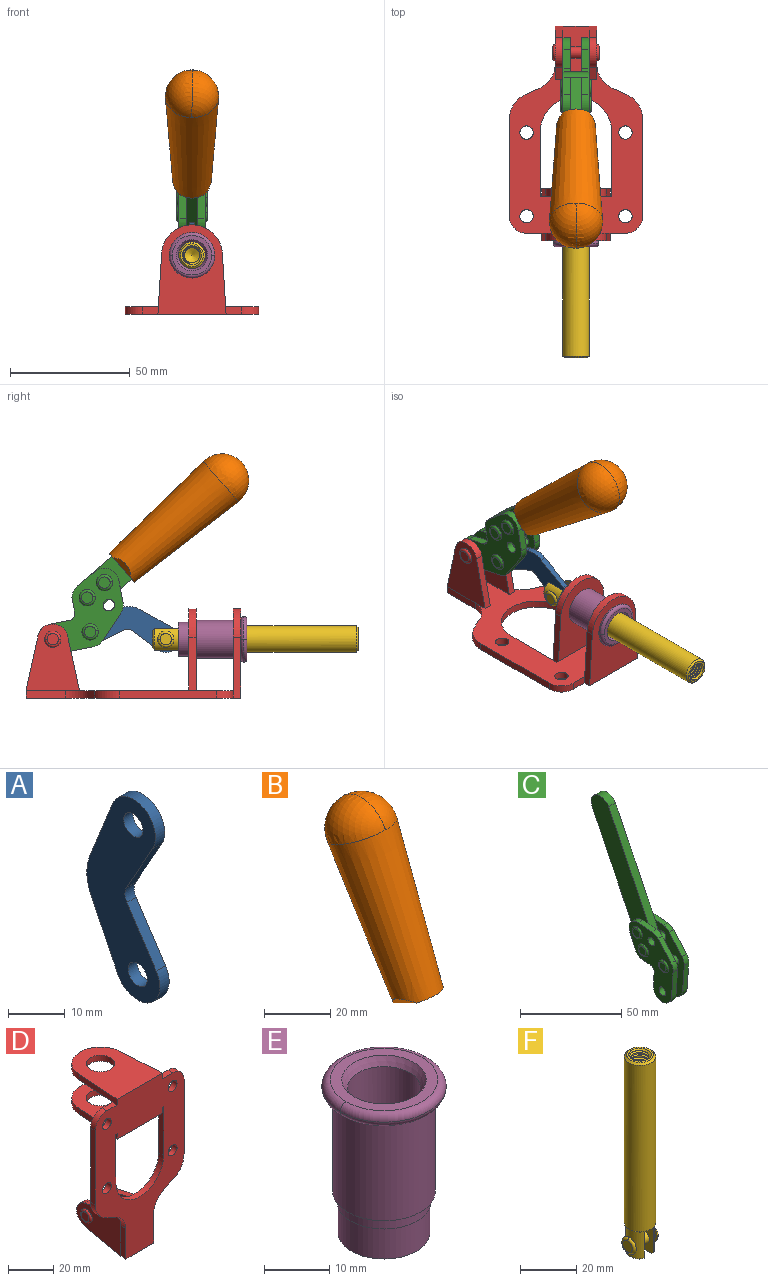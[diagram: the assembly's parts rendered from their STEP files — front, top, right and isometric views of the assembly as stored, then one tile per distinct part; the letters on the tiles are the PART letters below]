
ASSEMBLY  parts=6 mates=6
PART A: 12 faces, bbox 2.3x18.2x42.8 mm
  f0: cylinder r=2.4mm len=4.8mm, axis (1,0,0), area 34.9mm2, adj f4,f11
  f1: cylinder r=10.41mm len=8.47mm, axis (1,0,0), area 20.2mm2, adj f4,f9,f10,f11
  f2: cylinder r=3.05mm len=3.16mm, axis (1,0,0), area 7.7mm2, adj f4,f6,f7,f11
  f3: cylinder r=2.4mm len=4.8mm, axis (1,0,0), area 34.9mm2, adj f4,f11
  f4: plane 42.81x18.23mm, normal (-1,0,0), area 414.1mm2, adj f0,f1,f2,f3,f5,f6,f7,f8
  f5: cylinder r=5.54mm len=10.67mm, axis (1,0,0), area 41.8mm2, adj f4,f6,f10,f11
  f6: plane 11.66x6.53mm, normal (0,-0.87,-0.49), area 30.9mm2, adj f2,f4,f5,f11
  f7: plane 11.17x7.33mm, normal (0,-0.84,0.55), area 30.9mm2, adj f2,f4,f8,f11
  f8: cylinder r=5.54mm len=10.51mm, axis (1,0,0), area 41.8mm2, adj f4,f7,f9,f11
  f9: plane 13.67x6.67mm, normal (0,0.9,-0.44), area 35.1mm2, adj f1,f4,f8,f11
  f10: plane 14.1x5.7mm, normal (0,0.93,0.37), area 35.1mm2, adj f1,f4,f5,f11
  f11: plane 42.81x18.23mm, normal (1,0,0), area 414.1mm2, adj f0,f1,f2,f3,f5,f6,f7,f8
PART B: 11 faces, bbox 22.3x42.6x64.5 mm
  f0: sphere r=11.13mm, area 411.4mm2, adj f1,f8
  f1: cone r=11.11mm half-angle=3.3deg, axis (0,0.44,0.9), area 3251.8mm2, adj f0,f7,f8,f9,f10
  f2: cylinder r=6.16mm len=11.7mm, axis (1,0,0), area 89.5mm2, adj f3,f4,f5,f6
  f3: plane 60.23x36.75mm, normal (-1,0,0), area 763.6mm2, adj f2,f4,f6,f10
  f4: plane 51.37x25.05mm, normal (0,0.9,-0.44), area 264.2mm2, adj f2,f3,f5,f10
  f5: plane 60.23x36.75mm, normal (1,0,0), area 763.6mm2, adj f2,f4,f6,f10
  f6: plane 51.37x25.05mm, normal (0,-0.9,0.44), area 264.2mm2, adj f2,f3,f5,f10
  f7: plane 9.95x5.95mm, normal (0.71,-0.31,-0.64), area 25.8mm2, adj f1,f10
  f8: sphere r=11.13mm, area 411.4mm2, adj f0,f1
  f9: plane 9.95x5.95mm, normal (-0.71,-0.31,-0.64), area 25.8mm2, adj f1,f10
  f10: plane 14.27x11.38mm, normal (0,-0.44,-0.9), area 106.7mm2, adj f1,f3,f4,f5,f6,f7,f9
PART C: 59 faces, bbox 12.9x60.2x99.6 mm
  f0: torus R=2.39mm, axis (-1,0,0), area 14.9mm2, adj f20,f43,f51
  f1: torus R=2.39mm, axis (-1,0,0), area 14.9mm2, adj f19,f42,f51
  f2: torus R=2.39mm, axis (-1,0,0), area 14.9mm2, adj f18,f35,f51
  f3: torus R=2.39mm, axis (-1,0,0), area 14.9mm2, adj f14,f17,f23
  f4: torus R=2.39mm, axis (-1,0,0), area 14.9mm2, adj f13,f16,f23
  f5: torus R=2.39mm, axis (-1,0,0), area 14.9mm2, adj f12,f15,f23
  f6: cylinder r=2.39mm len=4.78mm, axis (1,0,0), area 46.5mm2, adj f48,f50,f51
  f7: cylinder r=2.39mm len=4.78mm, axis (1,0,0), area 46.5mm2, adj f50,f51
  f8: cylinder r=6.35mm len=12.68mm, axis (1,0,0), area 61.8mm2, adj f38,f39,f50,f51
  f9: cylinder r=2.39mm len=4.78mm, axis (-1,0,0), area 70.5mm2, adj f46,f50
  f10: cylinder r=2.39mm len=4.78mm, axis (-1,0,0), area 46.5mm2, adj f23,f45,f46
  f11: cylinder r=2.39mm len=4.78mm, axis (-1,0,0), area 46.5mm2, adj f23,f46
  f12: plane 4.78x4.78mm, normal (1,0,0), area 17.9mm2, adj f5,f15
  f13: plane 4.78x4.78mm, normal (1,0,0), area 17.9mm2, adj f4,f16
  f14: plane 4.78x4.78mm, normal (1,0,0), area 17.9mm2, adj f3,f17
  f15: torus R=2.39mm, axis (-1,0,0), area 14.9mm2, adj f5,f12,f23
  f16: torus R=2.39mm, axis (-1,0,0), area 14.9mm2, adj f4,f13,f23
  f17: torus R=2.39mm, axis (-1,0,0), area 14.9mm2, adj f3,f14,f23
  f18: plane 4.78x4.78mm, normal (-1,0,0), area 17.9mm2, adj f2,f35
  f19: plane 4.78x4.78mm, normal (-1,0,0), area 17.9mm2, adj f1,f42
  f20: plane 4.78x4.78mm, normal (-1,0,0), area 17.9mm2, adj f0,f43
  f21: plane 2.26x0.2mm, normal (1,0,0), area 0.2mm2, adj f31,f44
  f22: plane 2.26x0.2mm, normal (-1,0,0), area 0.2mm2, adj f41,f44
  f23: plane 39.37x30.77mm, normal (1,0,0), area 565.5mm2, adj f3,f4,f5,f10,f11,f15,f16,f17
  f24: cylinder r=6.1mm len=4.15mm, axis (-1,0,0), area 14.7mm2, adj f23,f25,f32,f46
  f25: plane 10.25x9.01mm, normal (0,-0.75,0.66), area 42.3mm2, adj f23,f24,f26,f46
  f26: cylinder r=6.35mm len=4.64mm, axis (-1,0,0), area 15.6mm2, adj f23,f25,f27,f46
  f27: plane 15.84x3.1mm, normal (0,-1,-0.07), area 49.2mm2, adj f23,f26,f28,f46
  f28: cylinder r=6.35mm len=12.68mm, axis (-1,0,0), area 61.8mm2, adj f23,f27,f29,f46
  f29: plane 8.11x3.1mm, normal (0,1,0.07), area 25.2mm2, adj f23,f28,f30,f46
  f30: cylinder r=3.05mm len=3.25mm, axis (-1,0,0), area 14.8mm2, adj f23,f29,f31,f46
  f31: plane 5.99x3.1mm, normal (0,0.07,-1), area 18.6mm2, adj f21,f23,f30,f44,f46
  f32: plane 9.5x3.1mm, normal (0,-0.07,1), area 29.5mm2, adj f23,f24,f33,f46,f47
  f33: cylinder r=6.1mm len=8.63mm, axis (-1,0,0), area 39.1mm2, adj f23,f32,f34,f47
  f34: plane 8.65x3.96mm, normal (0,0.91,-0.42), area 29.5mm2, adj f23,f33,f44,f47
  f35: torus R=2.39mm, axis (-1,0,0), area 14.9mm2, adj f2,f18,f51
  f36: plane 10.25x9.01mm, normal (0,-0.75,0.66), area 42.3mm2, adj f37,f49,f50,f51
  f37: cylinder r=6.35mm len=4.64mm, axis (1,0,0), area 15.6mm2, adj f36,f38,f50,f51
  f38: plane 15.84x3.1mm, normal (0,-1,-0.07), area 49.2mm2, adj f8,f37,f50,f51
  f39: plane 8.11x3.1mm, normal (0,1,0.07), area 25.2mm2, adj f8,f40,f50,f51
  f40: cylinder r=3.05mm len=3.25mm, axis (1,0,0), area 14.8mm2, adj f39,f41,f50,f51
  f41: plane 5.99x3.1mm, normal (0,0.07,-1), area 18.6mm2, adj f22,f40,f44,f50,f51
  f42: torus R=2.39mm, axis (-1,0,0), area 14.9mm2, adj f1,f19,f51
  f43: torus R=2.39mm, axis (-1,0,0), area 14.9mm2, adj f0,f20,f51
  f44: cylinder r=6.35mm len=12.12mm, axis (-1,0,0), area 128.9mm2, adj f21,f22,f23,f31,f34,f41,f46,f47
  f45: plane 2.65x1.35mm, normal (1,0,0), area 1mm2, adj f10,f55
  f46: plane 39.08x20.42mm, normal (-1,0,0), area 412.5mm2, adj f9,f10,f11,f24,f25,f26,f27,f28
  f47: plane 77.62x39.82mm, normal (1,0,0), area 850mm2, adj f32,f33,f34,f44,f53,f54,f55
  f48: plane 2.65x1.35mm, normal (-1,0,0), area 1mm2, adj f6,f55
  f49: cylinder r=6.1mm len=4.15mm, axis (1,0,0), area 14.7mm2, adj f36,f50,f51,f56
  f50: plane 39.08x20.42mm, normal (1,0,0), area 412.5mm2, adj f6,f7,f8,f9,f36,f37,f38,f39
  f51: plane 39.37x30.77mm, normal (-1,0,0), area 565.5mm2, adj f0,f1,f2,f6,f7,f8,f35,f36
  f52: plane 8.65x3.96mm, normal (0,0.91,-0.42), area 29.5mm2, adj f44,f51,f57,f58
  f53: plane 68.49x33.4mm, normal (0,0.9,-0.44), area 358.1mm2, adj f44,f47,f54,f58
  f54: cylinder r=6.35mm len=12.06mm, axis (1,0,0), area 93.7mm2, adj f47,f53,f55,f58
  f55: plane 68.49x33.4mm, normal (0,-0.9,0.44), area 358.1mm2, adj f44,f45,f46,f47,f48,f50,f54,f58
  f56: plane 9.5x3.1mm, normal (0,-0.07,1), area 29.5mm2, adj f49,f50,f51,f57,f58
  f57: cylinder r=6.1mm len=8.63mm, axis (1,0,0), area 39.1mm2, adj f51,f52,f56,f58
  f58: plane 77.62x39.82mm, normal (-1,0,0), area 850mm2, adj f44,f52,f53,f54,f55,f56,f57
PART D: 55 faces, bbox 55.7x37.4x89.8 mm
  f0: torus R=2.41mm, axis (-1,0,0), area 15mm2, adj f11,f15,f25
  f1: torus R=2.41mm, axis (-1,0,0), area 15mm2, adj f10,f12,f22
  f2: cylinder r=2.78mm len=5.56mm, axis (0,-1,0), area 54.2mm2, adj f30,f54
  f3: cylinder r=14.99mm len=29.97mm, axis (0,-1,0), area 145.9mm2, adj f30,f49,f53,f54
  f4: cylinder r=2.78mm len=5.56mm, axis (0,-1,0), area 54.2mm2, adj f30,f54
  f5: cylinder r=2.78mm len=5.56mm, axis (0,-1,0), area 54.2mm2, adj f30,f54
  f6: cylinder r=2.78mm len=5.56mm, axis (0,-1,0), area 54.2mm2, adj f30,f54
  f7: cylinder r=6.35mm len=12.7mm, axis (0,0,1), area 123.6mm2, adj f27,f51
  f8: cylinder r=6.35mm len=12.7mm, axis (0,0,-1), area 124.7mm2, adj f21,f35
  f9: cylinder r=2.41mm len=11.18mm, axis (-1,0,0), area 169.4mm2, adj f16,f19
  f10: plane 4.83x4.83mm, normal (1,0,0), area 18.3mm2, adj f1,f12
  f11: plane 4.83x4.83mm, normal (-1,0,0), area 18.3mm2, adj f0,f15
  f12: torus R=2.41mm, axis (-1,0,0), area 15mm2, adj f1,f10,f22
  f13: cylinder r=6.35mm len=12.41mm, axis (1,0,0), area 53.4mm2, adj f18,f19,f22,f23
  f14: cylinder r=6.35mm len=12.41mm, axis (-1,0,0), area 53.4mm2, adj f16,f17,f24,f25
  f15: torus R=2.41mm, axis (-1,0,0), area 15mm2, adj f0,f11,f25
  f16: plane 27.86x22.35mm, normal (1,0,0), area 425.4mm2, adj f9,f14,f17,f24,f30
  f17: plane 22.86x4.97mm, normal (0,0.21,0.98), area 72.5mm2, adj f14,f16,f25,f30
  f18: plane 22.86x4.97mm, normal (0,0.21,0.98), area 72.5mm2, adj f13,f19,f22,f30
  f19: plane 27.86x22.35mm, normal (-1,0,0), area 425.4mm2, adj f9,f13,f18,f23,f30
  f20: cylinder r=12.7mm len=25.35mm, axis (0,0,-1), area 119.8mm2, adj f21,f34,f35,f36
  f21: plane 34.21x28.07mm, normal (0,0,-1), area 702.4mm2, adj f8,f20,f30,f34,f36
  f22: plane 27.96x22.45mm, normal (1,0,0), area 407.2mm2, adj f1,f12,f13,f18,f23,f30,f42,f43
  f23: plane 22.86x4.97mm, normal (0,0.21,-0.98), area 72.5mm2, adj f13,f19,f22,f44
  f24: plane 22.86x4.97mm, normal (0,0.21,-0.98), area 72.5mm2, adj f14,f16,f25,f44
  f25: plane 27.86x22.35mm, normal (-1,0,0), area 407.1mm2, adj f0,f14,f15,f17,f24,f30,f45,f46
  f26: plane 3.1x0.95mm, normal (0,0,-1), area 2.7mm2, adj f30,f49,f50,f54
  f27: plane 34.21x28.07mm, normal (0,0,1), area 702.4mm2, adj f7,f28,f30,f50,f52
  f28: cylinder r=12.7mm len=25.35mm, axis (0,0,1), area 118.8mm2, adj f27,f50,f51,f52
  f29: plane 3.1x0.95mm, normal (0,0,-1), area 2.7mm2, adj f30,f52,f53,f54
  f30: plane 86.54x55.63mm, normal (0,1,0), area 2362.9mm2, adj f2,f3,f4,f5,f6,f16,f17,f18
  f31: plane 40.56x3.1mm, normal (-1,0,0), area 125.7mm2, adj f30,f32,f48,f54
  f32: cylinder r=7.11mm len=7.11mm, axis (0,-1,0), area 34.6mm2, adj f30,f31,f33,f54
  f33: plane 6.67x3.1mm, normal (0,0,1), area 20.4mm2, adj f30,f32,f34,f54
  f34: plane 25.39x3.13mm, normal (-1,0.06,0), area 79.5mm2, adj f20,f21,f33,f35,f54
  f35: plane 37.31x28.45mm, normal (0,0,1), area 789.9mm2, adj f8,f20,f34,f36,f54
  f36: plane 25.39x3.13mm, normal (1,0.06,0), area 79.5mm2, adj f20,f21,f35,f37,f54
  f37: plane 6.67x3.1mm, normal (0,0,1), area 20.4mm2, adj f30,f36,f38,f54
  f38: cylinder r=7.11mm len=7.11mm, axis (0,-1,0), area 34.6mm2, adj f30,f37,f39,f54
  f39: plane 40.56x3.1mm, normal (1,0,0), area 125.7mm2, adj f30,f38,f40,f54
  f40: cylinder r=11.18mm len=10.16mm, axis (0,-1,0), area 39.5mm2, adj f30,f39,f41,f54
  f41: plane 6.09x3.1mm, normal (0.42,0,-0.91), area 20.8mm2, adj f30,f40,f42,f54
  f42: cylinder r=11.18mm len=9.41mm, axis (0,-1,0), area 37.2mm2, adj f22,f30,f41,f43,f54
  f43: plane 16.5x3.1mm, normal (1,0,0), area 51.1mm2, adj f22,f42,f44,f54
  f44: plane 17.37x3.1mm, normal (0,0,-1), area 53.8mm2, adj f23,f24,f30,f43,f45,f54
  f45: plane 16.5x3.1mm, normal (-1,0,0), area 51.1mm2, adj f25,f44,f46,f54
  f46: cylinder r=11.18mm len=9.41mm, axis (0,-1,0), area 37.2mm2, adj f25,f30,f45,f47,f54
  f47: plane 6.09x3.1mm, normal (-0.42,0,-0.91), area 20.8mm2, adj f30,f46,f48,f54
  f48: cylinder r=11.18mm len=10.16mm, axis (0,-1,0), area 39.5mm2, adj f30,f31,f47,f54
  f49: plane 26.54x3.1mm, normal (-1,0,0), area 82.3mm2, adj f3,f26,f30,f54
  f50: plane 25.39x3.1mm, normal (1,0.06,0), area 78.8mm2, adj f26,f27,f28,f51,f54
  f51: plane 37.31x28.45mm, normal (0,0,-1), area 789.9mm2, adj f7,f28,f50,f52,f54
  f52: plane 25.39x3.1mm, normal (-1,0.06,0), area 78.8mm2, adj f27,f28,f29,f51,f54
  f53: plane 26.54x3.1mm, normal (1,0,0), area 82.3mm2, adj f3,f29,f30,f54
  f54: plane 89.66x55.63mm, normal (0,-1,0), area 2678.5mm2, adj f2,f3,f4,f5,f6,f26,f29,f31
PART E: 15 faces, bbox 20.6x20.6x28.7 mm
  f0: torus R=8.26mm, axis (0,0,1), area 56.8mm2, adj f1,f10,f12
  f1: torus R=8.26mm, axis (0,0,1), area 56.8mm2, adj f0,f6,f13
  f2: cylinder r=5.59mm len=25.91mm, axis (0,0,1), area 909.6mm2, adj f3,f4
  f3: cone r=6.86mm half-angle=45deg, axis (0,0,-1), area 70.2mm2, adj f2,f14
  f4: cone r=6.47mm half-angle=30deg, axis (0,0,1), area 66.7mm2, adj f2,f13
  f5: cylinder r=7.04mm len=14.07mm, axis (0,0,1), area 252.6mm2, adj f11,f14
  f6: torus R=8.26mm, axis (0,0,1), area 56.8mm2, adj f1,f12,f13
  f7: cylinder r=7.16mm len=14.33mm, axis (0,0,1), area 91.5mm2, adj f9,f11
  f8: cylinder r=7.86mm len=18.42mm, axis (0,0,1), area 909.6mm2, adj f9,f10
  f9: plane 15.72x15.72mm, normal (0,0,-1), area 33mm2, adj f7,f8
  f10: plane 16.51x16.51mm, normal (0,0,-1), area 19.9mm2, adj f0,f8,f12
  f11: plane 14.33x14.33mm, normal (0,0,-1), area 5.7mm2, adj f5,f7
  f12: torus R=8.26mm, axis (0,0,1), area 56.8mm2, adj f0,f6,f10
  f13: plane 16.51x16.51mm, normal (0,0,1), area 82.7mm2, adj f1,f4,f6
  f14: plane 14.07x14.07mm, normal (0,0,-1), area 7.8mm2, adj f3,f5
PART F: 48 faces, bbox 12.6x11.1x86.1 mm
  f0: torus R=2.41mm, axis (-1,0,0), area 15mm2, adj f30,f32,f34
  f1: torus R=2.41mm, axis (-1,0,0), area 15mm2, adj f29,f31,f33
  f2: cylinder r=5.54mm len=72.39mm, axis (0,0,1), area 2518.5mm2, adj f3,f4,f42,f43
  f3: cone r=5.54mm half-angle=45deg, axis (0,0,1), area 7.6mm2, adj f2,f5,f41
  f4: cone r=5.54mm half-angle=45deg, axis (0,0,-1), area 34.9mm2, adj f2,f39
  f5: cylinder r=5.08mm len=11.48mm, axis (0,0,1), area 108.3mm2, adj f3,f7,f8,f41
  f6: cylinder r=2.41mm len=4.83mm, axis (-1,0,0), area 71.2mm2, adj f40,f41
  f7: cylinder r=2.41mm len=4.83mm, axis (-1,0,0), area 7.6mm2, adj f5,f34
  f8: cone r=5.08mm half-angle=45deg, axis (0,0,1), area 10.6mm2, adj f5,f37,f41
  f9: cone r=3.98mm half-angle=45deg, axis (0,0,1), area 17.6mm2, adj f27,f39,f45,f46,f47
  f10: cylinder r=2.41mm len=4.83mm, axis (-1,0,0), area 7.6mm2, adj f33,f38
  f11: cylinder r=3.2mm len=6.4mm, axis (0,0,1), area 78.4mm2, adj f12,f28,f44,f45,f47
  f12: cylinder r=3.2mm len=6.4mm, axis (0,0,1), area 10.5mm2, adj f11,f13,f45,f47
  f13: cylinder r=3.2mm len=6.4mm, axis (0,0,1), area 10.5mm2, adj f12,f14,f45,f47
  f14: cylinder r=3.2mm len=6.4mm, axis (0,0,1), area 10.5mm2, adj f13,f15,f45,f47
  f15: cylinder r=3.2mm len=6.4mm, axis (0,0,1), area 10.5mm2, adj f14,f16,f45,f47
  f16: cylinder r=3.2mm len=6.4mm, axis (0,0,1), area 10.5mm2, adj f15,f17,f45,f47
  f17: cylinder r=3.2mm len=6.4mm, axis (0,0,1), area 10.5mm2, adj f16,f18,f45,f47
  f18: cylinder r=3.2mm len=6.4mm, axis (0,0,1), area 10.5mm2, adj f17,f19,f45,f47
  f19: cylinder r=3.2mm len=6.4mm, axis (0,0,1), area 10.5mm2, adj f18,f20,f45,f47
  f20: cylinder r=3.2mm len=6.4mm, axis (0,0,1), area 10.5mm2, adj f19,f21,f45,f47
  f21: cylinder r=3.2mm len=6.4mm, axis (0,0,1), area 10.5mm2, adj f20,f22,f45,f47
  f22: cylinder r=3.2mm len=6.4mm, axis (0,0,1), area 10.5mm2, adj f21,f23,f45,f47
  f23: cylinder r=3.2mm len=6.4mm, axis (0,0,1), area 10.5mm2, adj f22,f24,f45,f47
  f24: cylinder r=3.2mm len=6.4mm, axis (0,0,1), area 10.5mm2, adj f23,f25,f45,f47
  f25: cylinder r=3.2mm len=6.4mm, axis (0,0,1), area 10.5mm2, adj f24,f26,f45,f47
  f26: cylinder r=3.2mm len=6.4mm, axis (0,0,1), area 10.5mm2, adj f25,f27,f45,f47
  f27: cylinder r=3.2mm len=6.4mm, axis (0,0,1), area 7.4mm2, adj f9,f26,f45,f47
  f28: cone r=3.2mm half-angle=60deg, axis (0,0,1), area 37.2mm2, adj f11
  f29: plane 4.83x4.83mm, normal (-1,0,0), area 18.3mm2, adj f1,f31
  f30: plane 4.83x4.83mm, normal (1,0,0), area 18.3mm2, adj f0,f32
  f31: torus R=2.41mm, axis (-1,0,0), area 15mm2, adj f1,f29,f33
  f32: torus R=2.41mm, axis (-1,0,0), area 15mm2, adj f0,f30,f34
  f33: plane 6.83x6.83mm, normal (1,0,0), area 18.3mm2, adj f1,f10,f31
  f34: plane 6.83x6.83mm, normal (-1,0,0), area 18.3mm2, adj f0,f7,f32
  f35: cone r=5.08mm half-angle=45deg, axis (0,0,1), area 10.6mm2, adj f36,f38,f40
  f36: plane 7.25x1.97mm, normal (0,0,-1), area 10mm2, adj f35,f40
  f37: plane 7.25x1.97mm, normal (0,0,-1), area 10mm2, adj f8,f41
  f38: cylinder r=5.08mm len=11.48mm, axis (0,0,1), area 108.3mm2, adj f10,f35,f40,f42
  f39: plane 9.55x9.55mm, normal (0,0,1), area 22mm2, adj f4,f9
  f40: plane 12.76x10.09mm, normal (1,0,0), area 95.7mm2, adj f6,f35,f36,f38,f42,f43
  f41: plane 12.76x10.09mm, normal (-1,0,0), area 95.7mm2, adj f3,f5,f6,f8,f37,f43
  f42: cone r=5.54mm half-angle=45deg, axis (0,0,1), area 7.6mm2, adj f2,f38,f40
  f43: plane 11.07x4.7mm, normal (0,0,-1), area 50.4mm2, adj f2,f40,f41
  f44: plane 0.89x0.62mm, normal (-1,0,0), area 0.3mm2, adj f11,f45,f46,f47
  f45: bspline ~24.8x7.63mm, area 266.6mm2, adj f9,f11,f12,f13,f14,f15,f16,f17
  f46: bspline ~24.87x7.63mm, area 73.6mm2, adj f9,f44,f45,f47
  f47: bspline ~24.98x7.63mm, area 272.5mm2, adj f9,f11,f12,f13,f14,f15,f16,f17
PLACE A rot(axis=(1,0,0),97.5deg) t=(0,12.59,2.22)mm
PLACE B rot(axis=(1,0,0),75deg) t=(0,3.86,9.14)mm
PLACE C rot(axis=(1,0,0),75deg) t=(0,3.86,9.14)mm
PLACE D rot(axis=(1,0,0),90deg) t=(0,9.14,0)mm fixed
PLACE E rot(axis=(1,0,0),90deg) t=(0,9.14,0)mm
PLACE F rot(axis=(1,0,0),90deg) t=(0,9.52,0)mm
MATE revolute A.f5 <-> F.f6  axis (1,0,0) through (0,-5.96,24.61)mm
MATE fastened C.f54 <-> B.f2  axis (1,0,0) through (0,-30.66,91.94)mm
MATE revolute A.f3 <-> C.f4  axis (1,0,0) through (0,25.65,27.64)mm
MATE revolute D.f0 <-> C.f7  axis (-1,0,0) through (0,41.23,24.61)mm
MATE slider F.f2 <-> D.f7  axis (0,-1,0) through (0,-49.26,24.61)mm
MATE fastened D.f7 <-> E.f0  axis (0,-1,0) through (0,-37.25,24.61)mm
